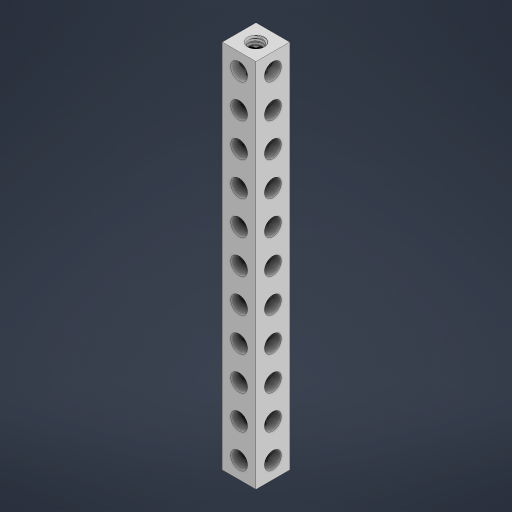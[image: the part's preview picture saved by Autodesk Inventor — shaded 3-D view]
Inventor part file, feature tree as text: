
AUTODESK INVENTOR PART (.ipt)
format: ipt  version: 2023 (Build 270158000, 158)  size: 1,394,688 bytes
history: native  units: in
note: dims shown in document units (in); Inventor stores cm internally (conversion verified against a paired STEP export)
features: mirror x1
ambient origin geometry x8: Origin, YZ Plane, XZ Plane, XY Plane, X Axis, Y Axis, Z Axis, Center Point
bodies: Solid1 (feature_tree)
feature tree (1):
  mirror  "Mirror3"
